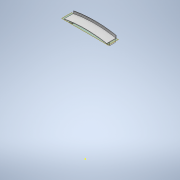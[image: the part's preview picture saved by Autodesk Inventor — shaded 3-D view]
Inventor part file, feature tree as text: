
AUTODESK INVENTOR PART (.ipt)
format: ipt  version: 2020.2 (Build 242310000, 310)  size: 196,608 bytes
history: native  units: mm
features: sketch x8, extrude x7, other x1
ambient origin geometry x8: Origin, YZ Plane, XZ Plane, XY Plane, X Axis, Y Axis, Z Axis, Center Point
bodies: Solide1 (feature_tree)
feature tree (16):
  extrude  "Extrusion1"  Depth=785.7mm
  other  "Plan de construction1"
  extrude  "Extrusion2"  Depth=3.0mm
  extrude  "Extrusion3"  Depth=14.3mm
  sketch  "Esquisse9"
  extrude  "Extrusion4"  Depth=65.0mm TaperAngle=0.0deg
  extrude  "Extrusion5"  Depth=20.0mm
  extrude  "Extrusion6"  Depth=35.0mm
  extrude  "Extrusion7"  Depth=8.0mm
  sketch  "Esquisse1"
  sketch  "Esquisse4"
  sketch  "Esquisse5"
  sketch  "Esquisse10"
  sketch  "Esquisse11"
  sketch  "Esquisse12"
  sketch  "Esquisse13"
